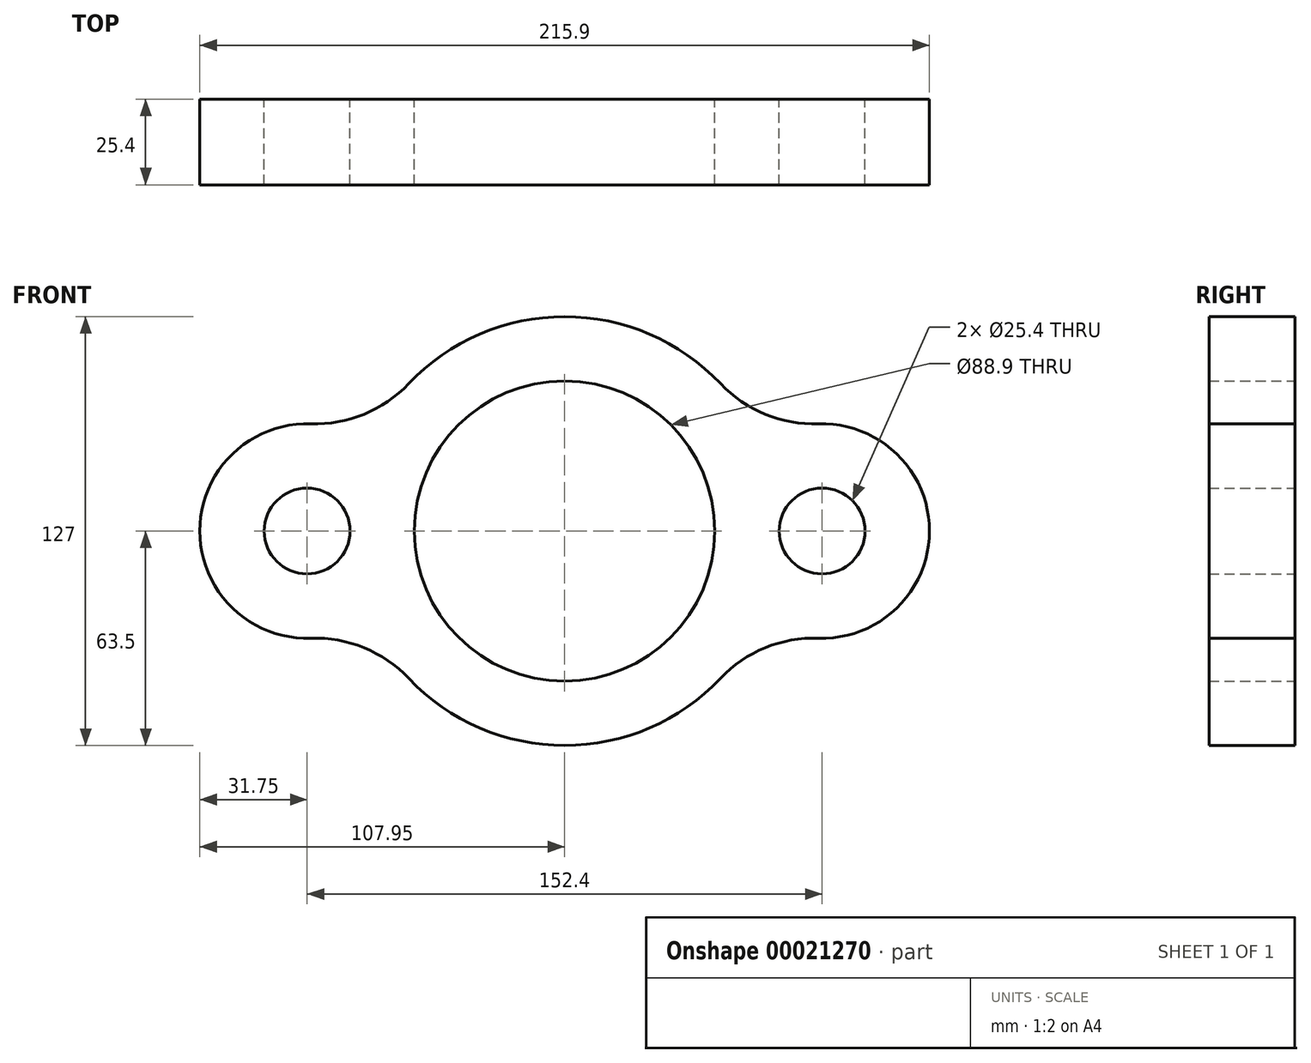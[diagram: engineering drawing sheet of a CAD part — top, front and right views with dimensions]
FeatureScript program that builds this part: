
annotation { "Feature Type Name" : "Feature", "Feature Type Description" : "" }
export const myFeature = defineFeature(function(context is Context, id is Id, definition is map)
    precondition{}
    {
        {
            var Q0;
            Q0=qCreatedBy(makeId("Front.planeOp"),FACE);
            var sketch = newSketch(context, id + "F0", { "sketchPlane" : qUnion([Q0])});
            skCircle(sketch, "E0", {"center": v(0, 0) * mm, "radius": 44.45 * mm});
            skArc(sketch, "E1", {"start": v(-46.14, -43.63) * mm, "mid": v(0, -63.5) * mm, "end": v(46.14, -43.63) * mm});
            skLineSegment(sketch, "E2", {"start": v(44.45, 0) * mm, "end": v(76.2, 0) * mm});
            skCircle(sketch, "E3", {"center": v(-76.2, 0) * mm, "radius": 12.7 * mm});
            skCircle(sketch, "E4", {"center": v(76.2, 0) * mm, "radius": 12.7 * mm});
            skArc(sketch, "E5", {"start": v(-75.12, 31.73) * mm, "mid": v(-107.95, 0) * mm, "end": v(-75.12, -31.73) * mm});
            skArc(sketch, "E6", {"start": v(75.12, -31.73) * mm, "mid": v(107.95, 0) * mm, "end": v(75.12, 31.73) * mm});
            skArc(sketch, "E7.trimOffspring", {"start": v(46.14, 43.63) * mm, "mid": v(0, 63.5) * mm, "end": v(-46.14, 43.63) * mm});
            skPoint(sketch, "E8.visualSharp", {"position": v(-57.94, 25.98) * mm});
            skArc(sketch, "E8.filletArc", {"start": v(-75.12, 31.73) * mm, "mid": v(-59.35, 34.56) * mm, "end": v(-46.14, 43.63) * mm});
            skPoint(sketch, "E9.visualSharp", {"position": v(-57.94, -25.98) * mm});
            skArc(sketch, "E9.filletArc", {"start": v(-46.14, -43.63) * mm, "mid": v(-59.35, -34.56) * mm, "end": v(-75.12, -31.73) * mm});
            skPoint(sketch, "E10.visualSharp", {"position": v(57.94, -25.98) * mm});
            skArc(sketch, "E10.filletArc", {"start": v(75.12, -31.73) * mm, "mid": v(59.35, -34.56) * mm, "end": v(46.14, -43.63) * mm});
            skPoint(sketch, "E11.visualSharp", {"position": v(57.94, 25.98) * mm});
            skArc(sketch, "E11.filletArc", {"start": v(46.14, 43.63) * mm, "mid": v(59.35, 34.56) * mm, "end": v(75.12, 31.73) * mm});
            skSolve(sketch);
        }
        {
            var Q0;
            Q0=makeQuery(id+"F0.imprint","IMPRINT",FACE,{"disambiguationData":[TD([[makeQuery(id+"F0.imprint","IMPRINT",EDGE,{"derivedFrom":sQuery(id+"F0.wireOp",EDGE,"E0")}),-1.0]])]});
            extrude(context, id + "F1", {"entities" : qUnion([Q0]), "depth" : 25.4 * mm});
        }
    });
